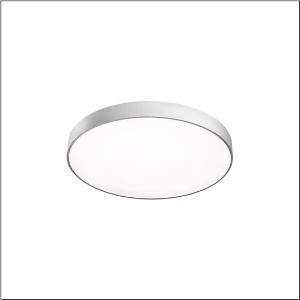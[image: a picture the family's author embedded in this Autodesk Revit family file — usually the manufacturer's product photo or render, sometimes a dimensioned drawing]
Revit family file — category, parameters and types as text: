
# Revit family: round_21_m_51mr36gm8321s
name_source: partatom
category: Lighting Fixtures
units: mm (PartAtom-declared; Revit-internal decimal feet)

## family parameters
Cut with Voids When Loaded = No
Host = Face
Light Source = No
Part Type = Normal
Room Calculation Point = No
Round Connector Dimension = Use Diameter
Shared = No

## types (1)
- --- (1 x LED, 8610 lm, 62.3 W, 3000K)
    Apparent Load = 62 VA
    CIE Flux Codes = 49 80 96 85 100
    Color Rendering = 80
    Color Temperature = 3000K
    Default Elevation = 1800 mm
    Description = Round 21 M, wall and ceiling luminaire, primary optical cover: cover, of PMMA, opal, light emission: direct/indirect distribution, primary light characteristic: symmetric, installation type: suspended mounting, surface-mounted, LED, rated luminous flux: 8.600lm, luminous efficacy: 138lm/W, light colour: 830, colour temperature: 3000K, control gear: ON/OFF Multilumen, with terminal, 3-pole, mains connection: 230V, AC, 50/60Hz, rated input power: 62.3W, housing, of aluminium, coated, silver, diameter: 600mm, height: 62mm, protection rating (complete): IP40, insulation class (complete): insulation class I (protective earthing), certification: CE, impact resistance: IK04, permissible operating ambient temperature: -10..+35°C, packaging unit: 1 piece
    Height = 87 mm
    Lamp = 1 x LED
    Lamp Light Flux = 8610 lm
    Lamp Power = 62.3 W
    Lamp count = 1
    Length = 600 mm
    Luminous efficacy = 138 lm/W
    Manufacturer = Siteco
    ModVariant = No
    Model = 51MR36GM8321S
    Mounting Place = Ceiling
    Mounting Type = Surface mounted
    Number of Poles = 1
    OnlyDefault = Yes
    Power Factor = 1
    Product Name = Round 21 M
    Product group = wall and ceiling luminaire | ceiling mounted
    ProductGroupID = 304
    Protection Class = Protection class I
    Protection Degree = IP 40
    RLX_Detail_Level = 1
    RLX_Emergency_Light_Flux = 0 lm
    RLX_Emergency_Type = 0
    RLX_Emergency_Type_DB = No
    RlxData = <blob elided: 17949 chars, md5=9bb5f8c6>
    Socket = socket
    Standby Power = 0 W
    System Light Flux = 8610 lm
    System Power = 62 W
    Type Comments = factory setting: luminous flux: 100 % | (ON | ON | ON | ON) | 700 mA
    Type Image = l_1258303.jpg
    URL = http://relux.com
    VarID = @adj_041151
    Voltage = 0 V
    Weight = 0.00 kg
    Width = 0 mm  [stored 0 ft]

note: [stored X ft] marks values corroborated as IEEE doubles in the binary element streams (Revit-internal decimal feet)

## geometry (parser evidence)
native form markers: Blend x4, Sweep x12
no freeform markers — native parametric forms only
